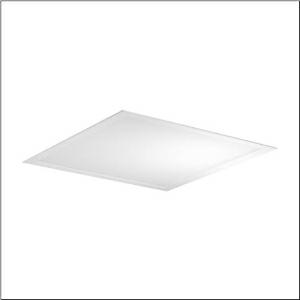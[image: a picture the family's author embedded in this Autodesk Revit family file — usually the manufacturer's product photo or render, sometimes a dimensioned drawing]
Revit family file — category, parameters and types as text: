
# Revit family: apollon_21_square_51mq11wd2614
name_source: partatom
category: Lighting Fixtures
units: mm (PartAtom-declared; Revit-internal decimal feet)

## family parameters
Cut with Voids When Loaded = No
Host = Face
Light Source = No
Part Type = Normal
Room Calculation Point = No
Round Connector Dimension = Use Diameter
Shared = No

## types (1)
- Apollon 21 square (1 x LED, 4150 lm, 24.7 W, 6500K)
    Apparent Load = 25 VA
    CIE Flux Codes = 60 87 97 100 100
    Color Rendering = 80
    Color Temperature = 6500K
    Default Elevation = 1800 mm
    Description = Apollon 21 square, office luminaire, primary optical cover: micro prismatic cover, of PMMA, CAT 2 (L<= 3000cd/m²), light emission: direct distribution, primary light characteristic: symmetric, installation type: lay-in mounting, recessed, LED, rated luminous flux: 4.150lm, luminous efficacy: 168lm/W, light colour: 865, colour temperature: 6500K, control gear: DALI 2, Multilumen, with terminal, 5-pole, mains connection: 220..240V, AC/DC, 0/50..60Hz, rated input power: 24.7W, suitable for self-contained emergency lighting element 59MQE002602A with integrated self-test function according to EN 60598-2-22, housing, of aluminium, coated, traffic white (RAL 9016), module: M625, length: 620mm, width: 620mm, height: 55mm, housing upper side, of sheet steel, galvanised, protection rating (complete): IP20, protection rating (lamp compartment, on room side): IP50, insulation class (complete): insulation class II (safety insulation), certification: CE, ENEC, UKCA, impact resistance: IK03, permissible operating ambient temperature: -20..+45°C, standard: EN 60598-2-22, corresponds to IFS (International Featured Standards) requirements for safety and quality in the food industry, packaging unit: 1 piece
    Height = 0 mm  [stored 0 ft]
    Lamp = 1 x LED
    Lamp Light Flux = 4150 lm
    Lamp Power = 24.7 W
    Lamp count = 1
    Length = 620 mm
    Luminous efficacy = 168 lm/W
    Manufacturer = Siteco
    ModVariant = No
    Model = 51MQ11WD2614
    Mounting Place = Ceiling
    Mounting Type = Recessed
    Number of Poles = 1
    OnlyDefault = Yes
    Power Factor = 1
    Product Name = Apollon 21 square
    Product group = office luminaire | ceiling recessed
    ProductGroupID = 400
    Protection Class = Protection class II
    Protection Degree = IP 20
    RLX_Detail_Level = 1
    RLX_Emergency_Light_Flux = 0 lm
    RLX_Emergency_Type = 0
    RLX_Emergency_Type_DB = No
    RlxData = <blob elided: 13301 chars, md5=2c9e3ebf>
    Socket = socket
    Standby Power = 0 W
    System Light Flux = 4150 lm
    System Power = 25 W
    Type Comments = Product without accessories
    Type Image = l_1291054.jpg
    URL = http://relux.com
    VarID = ---
    Voltage = 0 V
    Weight = 0.00 kg
    Width = 620 mm

note: [stored X ft] marks values corroborated as IEEE doubles in the binary element streams (Revit-internal decimal feet)

## geometry (parser evidence)
native form markers: Sweep x10
no freeform markers — native parametric forms only
